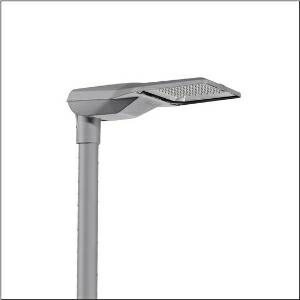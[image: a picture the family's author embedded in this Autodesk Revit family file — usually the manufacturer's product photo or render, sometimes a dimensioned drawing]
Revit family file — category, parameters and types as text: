
# Revit family: streetlight_sl_21_iq_midi___st0_5a_5xe3b41d08nb_db24
name_source: partatom
category: Lighting Fixtures
units: mm (PartAtom-declared; Revit-internal decimal feet)

## family parameters
Cut with Voids When Loaded = No
Host = Face
Light Source = No
Part Type = Normal
Room Calculation Point = No
Round Connector Dimension = Use Diameter
Shared = No

## types (1)
- --- (1 x LED, 24250 lm, 155.5 W, 4000K)
    Apparent Load = 155 VA
    CIE Flux Codes = 43 76 97 100 100
    Color Rendering = 70
    Color Temperature = 4000K
    Default Elevation = 1800 mm
    Description = Streetlight SL 21 iQ midi, mast luminaire, primary light control with lens, of PMMA, primary optical cover: cover, of toughened safety glass, transparent, light distribution: ST0.5a, light emission: direct distribution, primary light characteristic: asymmetric, installation type: post-top, side-entry, LED, High Power LED, rated luminous flux: 24.250lm, luminous efficacy: 156lm/W, light colour: 740, colour temperature: 4000K, control gear: iQ-Comfort, control: Auto-Match, Temp-Guard, Lumen-Switch, Night-Set, Smart-Wire, Light-Fading, Desk-Remote (wireless, voltage-free reading and setting of iQ features in the workshop via application-optimized NFC function/RFID function), optimised constant luminous flux control (CLO 2.0), pre-setting: linear dimming characteristic, mains connection: 230..240V, AC, 50/60Hz, start of lifetime: 156W, end of service life: 162W, reduction: 69W, luminaire housing, of diecast aluminium, powder-coated, Siteco® metallic grey (DB 702S), corrosivity category C5 mid according to DIN EN ISO 12944, please order mast flange separately, inclination adjustable: 0°, 5°, 10°, 15°, sealing non-destructively replaceable, multi-level sealing system, length: 644mm, width: 335mm, height: 110mm, mast flange for spigot size: 42mm (side-entry): 5XC10008XM4, 60/48mm (side-entry/post-top): 5XC10108XM2, 76/60mm (side-entry/post-top): 5XC10108XM1, mounting height: 4..8m, protection rating (complete): IP66, insulation class (complete): insulation class II (safety insulation), certification: CE, ENEC, ENEC+, VDE, impact resistance: IK10, permissible operating ambient temperature for outdoor applications: -40..+50°C, standard-compliant lighting for roads and squares, packaging unit: 1 piece

Light Distribution: ST0.5a
    Height = 111 mm
    Lamp = 1 x LED
    Lamp Light Flux = 24250 lm
    Lamp Power = 155.5 W
    Lamp count = 1
    Length = 644 mm
    Luminous efficacy = 156 lm/W
    Manufacturer = Siteco
    ModVariant = No
    Model = 5XE3B41D08NB
    Number of Poles = 1
    OnlyDefault = Yes
    Power Factor = 1
    Product Name = Streetlight SL 21 iQ midi | ST0.5a
    Product group = mast luminaire | pylon top
    ProductGroupID = 6100
    Protection Class = Protection class II
    Protection Degree = IP 66
    RLX_Detail_Level = 1
    RLX_Emergency_Light_Flux = 0 lm
    RLX_Emergency_Type = 0
    RLX_Emergency_Type_DB = No
    RlxData = <blob elided: 38461 chars, md5=52e3d5c4>
    Socket = socket
    Standby Power = 0 W
    System Light Flux = 24250 lm
    System Power = 155 W
    Type Comments = factory setting: luminous flux: 100 % | dim-lin: 254 | 823 mA
    Type Image = l_1004298.jpg
    URL = http://relux.com
    VarID = @adj_192971
    Voltage = 0 V
    Weight = 0.00 kg
    Width = 336 mm

## geometry (parser evidence)
native form markers: Blend x4, Sweep x11
no freeform markers — native parametric forms only
